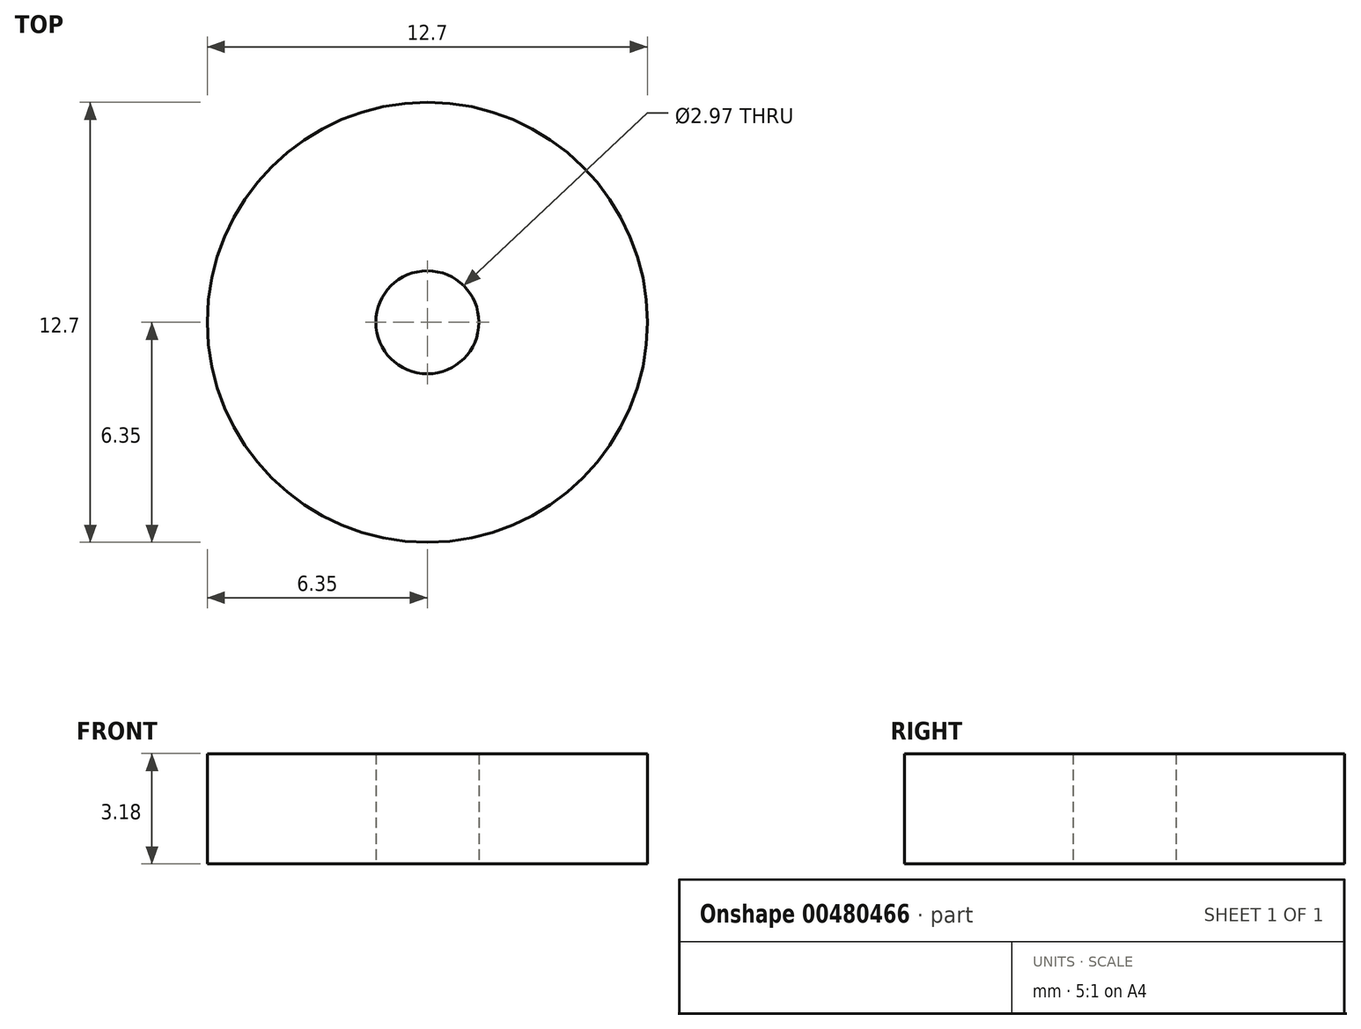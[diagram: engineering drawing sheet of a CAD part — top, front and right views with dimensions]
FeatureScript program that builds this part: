
annotation { "Feature Type Name" : "Feature", "Feature Type Description" : "" }
export const myFeature = defineFeature(function(context is Context, id is Id, definition is map)
    precondition{}
    {
        {
            var Q0;
            Q0=qCreatedBy(makeId("Top.planeOp"),FACE);
            var sketch = newSketch(context, id + "F0", { "sketchPlane" : qUnion([Q0])});
            skCircle(sketch, "E0", {"center": v(0, 0) * mm, "radius": 6.35 * mm});
            skCircle(sketch, "E1", {"center": v(0, 0) * mm, "radius": 1.49 * mm});
            skSolve(sketch);
        }
        {
            var Q0;
            Q0=makeQuery(id+"F0.imprint","IMPRINT",FACE,{"disambiguationData":[TD([[makeQuery(id+"F0.imprint","IMPRINT",EDGE,{"derivedFrom":sQuery(id+"F0.wireOp",EDGE,"E0")}),1.0]])]});
            extrude(context, id + "F1", {"entities" : qUnion([Q0]), "depth" : 3.17 * mm});
        }
    });
